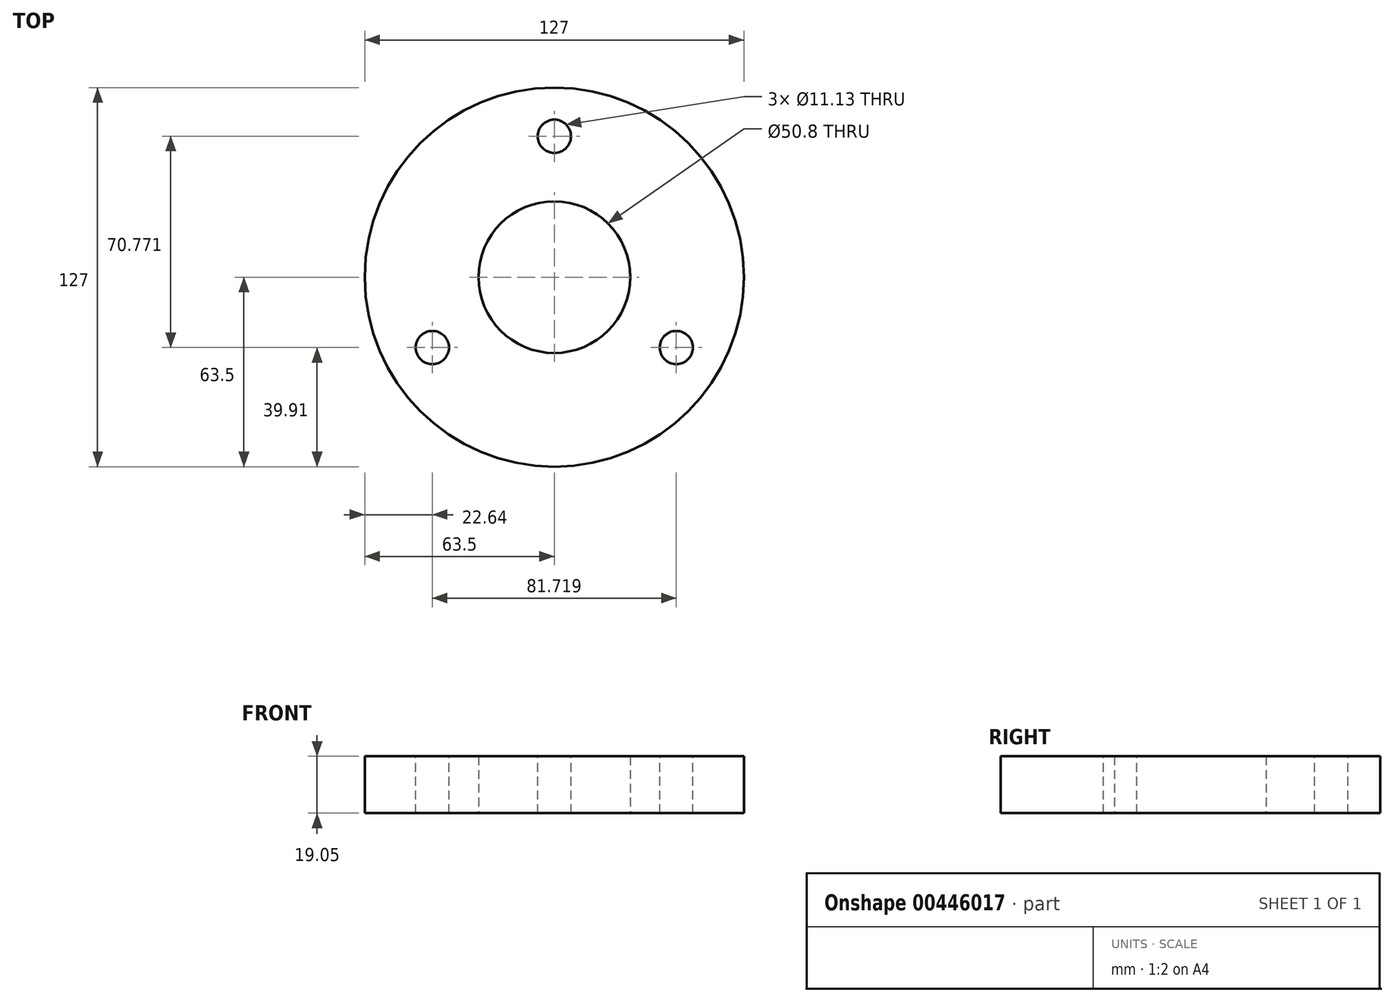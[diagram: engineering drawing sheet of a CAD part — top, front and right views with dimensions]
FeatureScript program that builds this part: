
annotation { "Feature Type Name" : "Feature", "Feature Type Description" : "" }
export const myFeature = defineFeature(function(context is Context, id is Id, definition is map)
    precondition{}
    {
        {
            var Q0;
            Q0=qCreatedBy(makeId("Top.planeOp"),FACE);
            var sketch = newSketch(context, id + "F0", { "sketchPlane" : qUnion([Q0])});
            skCircle(sketch, "E0", {"center": v(0, 0) * mm, "radius": 63.5 * mm});
            skCircle(sketch, "E1", {"center": v(0, 0) * mm, "radius": 25.4 * mm});
            skSolve(sketch);
        }
        {
            var Q0;
            Q0=qSketchRegion(id+"F0",true);
            extrude(context, id + "F1", {"entities" : qUnion([Q0]), "depth" : 19.05 * mm});
        }
        {
            var Q0;
            Q0=makeQuery(id+"F1.opExtrude","CAP_FACE",FACE,{"disambiguationData":[OSD([sQuery(id+"F0.wireOp",EDGE,"E0"),sQuery(id+"F0.wireOp",EDGE,"E1")])],"isStart":false});
            var sketch = newSketch(context, id + "F2", { "sketchPlane" : qUnion([Q0])});
            skCircle(sketch, "E2", {"center": v(0, 0) * mm, "radius": 47.18 * mm, "construction": true});
            skCircle(sketch, "E3", {"center": v(0, 47.18) * mm, "radius": 5.57 * mm});
            skCircle(sketch, "E4", {"center": v(-40.86, -23.6) * mm, "radius": 5.57 * mm});
            skCircle(sketch, "E5", {"center": v(40.86, -23.6) * mm, "radius": 5.57 * mm});
            skLineSegment(sketch, "E6", {"start": v(0, 0) * mm, "end": v(-40.86, -23.6) * mm, "construction": true});
            skLineSegment(sketch, "E7", {"start": v(0, 0) * mm, "end": v(40.86, -23.6) * mm, "construction": true});
            skLineSegment(sketch, "E8", {"start": v(0, 0) * mm, "end": v(0, -56.55) * mm, "construction": true});
            skSolve(sketch);
        }
        {
            var Q0;
            Q0=qSketchRegion(id+"F2",true);
            extrude(context, id + "F3", {"entities" : qUnion([Q0]), "operationType" : NewBodyOperationType.REMOVE, "oppositeDirection" : true, "depth" : 25.4 * mm});
        }
    });
